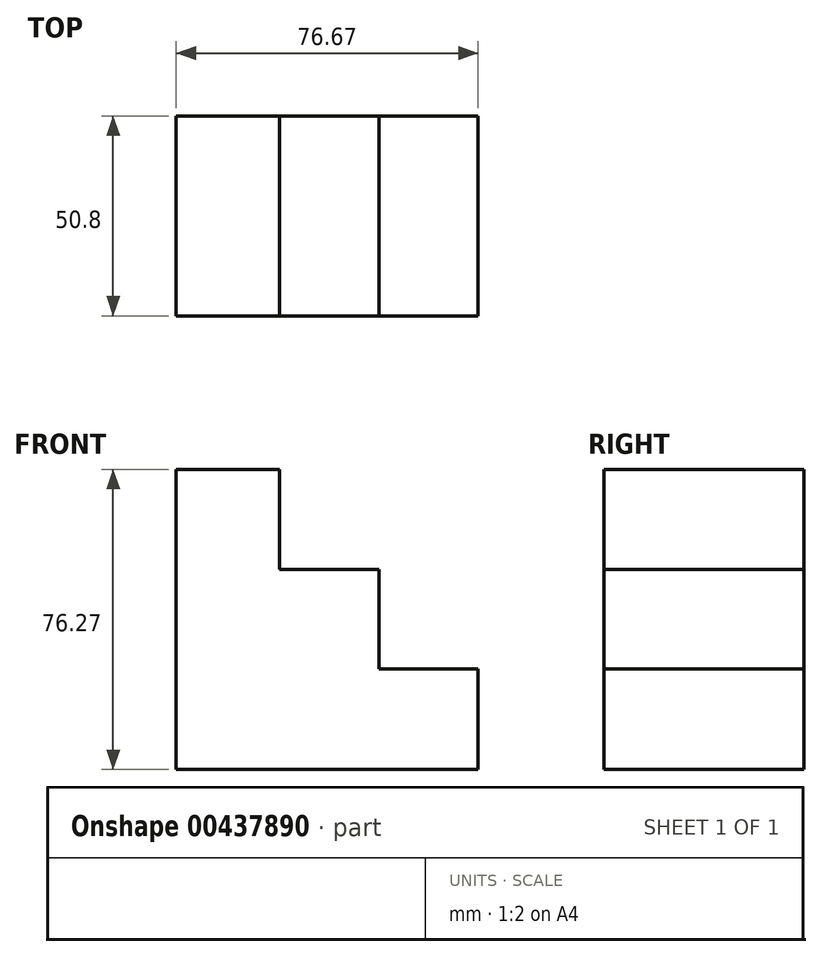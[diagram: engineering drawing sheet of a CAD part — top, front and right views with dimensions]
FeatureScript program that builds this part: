
annotation { "Feature Type Name" : "Feature", "Feature Type Description" : "" }
export const myFeature = defineFeature(function(context is Context, id is Id, definition is map)
    precondition{}
    {
        {
            var Q0;
            Q0=qCreatedBy(makeId("Front.planeOp"),FACE);
            var sketch = newSketch(context, id + "F0", { "sketchPlane" : qUnion([Q0])});
            skLineSegment(sketch, "E0", {"start": v(0, 0) * mm, "end": v(-76.67, 0) * mm});
            skLineSegment(sketch, "E1", {"start": v(-76.67, 0) * mm, "end": v(-76.67, 76.27) * mm});
            skLineSegment(sketch, "E2", {"start": v(-76.67, 76.27) * mm, "end": v(-50.5, 76.27) * mm});
            skLineSegment(sketch, "E3", {"start": v(-50.5, 76.27) * mm, "end": v(-50.5, 50.9) * mm});
            skLineSegment(sketch, "E4", {"start": v(-50.5, 50.9) * mm, "end": v(-25.11, 50.9) * mm});
            skLineSegment(sketch, "E5", {"start": v(-25.11, 50.9) * mm, "end": v(-25.11, 25.51) * mm});
            skLineSegment(sketch, "E6", {"start": v(-25.11, 25.51) * mm, "end": v(0, 25.51) * mm});
            skLineSegment(sketch, "E7", {"start": v(0, 25.51) * mm, "end": v(0, 0) * mm});
            skSolve(sketch);
        }
        {
            var Q0;
            Q0 = qSketchRegion(id + "F0", true);
            extrude(context, id + "F1", {"entities" : qUnion([Q0]), "depth" : 50.8 * mm});
        }
    });
